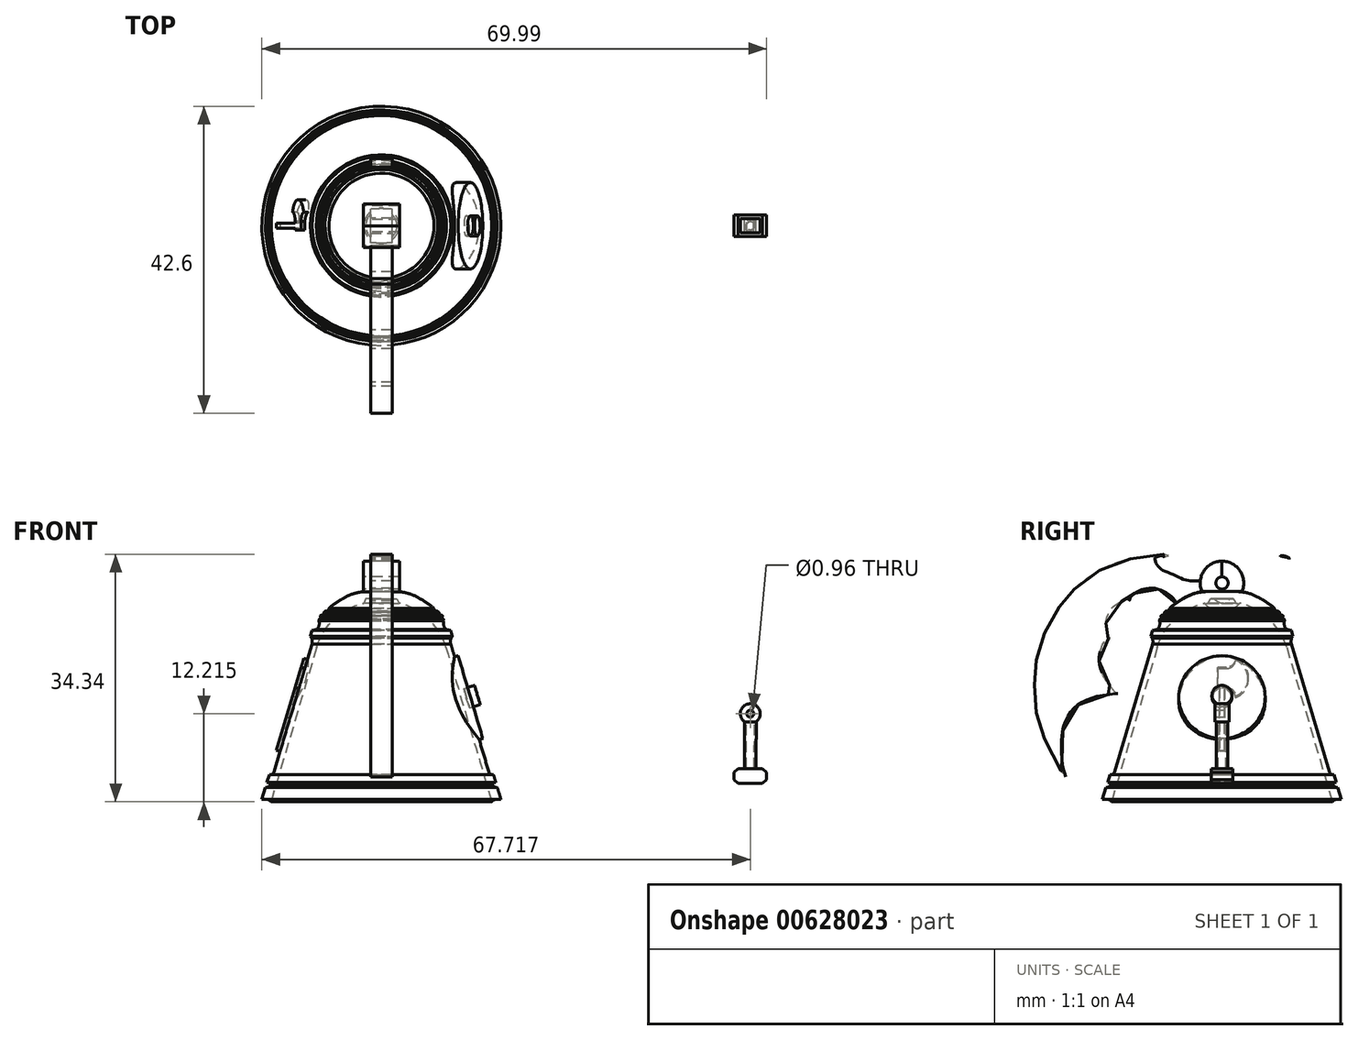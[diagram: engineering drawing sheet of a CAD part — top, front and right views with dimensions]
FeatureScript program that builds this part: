
annotation { "Feature Type Name" : "Feature", "Feature Type Description" : "" }
export const myFeature = defineFeature(function(context is Context, id is Id, definition is map)
    precondition{}
    {
        {
            var Q0;
            Q0=qCreatedBy(makeId("Front.planeOp"),FACE);
            var sketch = newSketch(context, id + "F0", { "sketchPlane" : qUnion([Q0])});
            skLineSegment(sketch, "E0", {"start": v(-8.59, 10.1) * mm, "end": v(-8.67, 9.83) * mm});
            skArc(sketch, "E1", {"start": v(-5.15, 13.04) * mm, "mid": v(-6.25, 12.35) * mm, "end": v(-7.29, 11.58) * mm});
            skFitSpline(sketch, "E2", {"points": [v(-8.38, 10.64) * mm, v(-8.4, 10.62) * mm, v(-8.42, 10.6) * mm, v(-8.44, 10.56) * mm, v(-8.46, 10.52) * mm, v(-8.47, 10.5) * mm], "startDerivative": vector(-0.14, -0.15) * mm, "endDerivative": vector(-0.05, -0.19) * mm});
            skArc(sketch, "E3", {"start": v(-15.49, -15.03) * mm, "mid": v(-15.75, -14.94) * mm, "end": v(-16.03, -14.94) * mm});
            skArc(sketch, "E4", {"start": v(-8.59, 10.1) * mm, "mid": v(-8.44, 10.27) * mm, "end": v(-8.47, 10.5) * mm});
            skLineSegment(sketch, "E5.trimOffspring", {"start": v(0, 13.78) * mm, "end": v(0, -14.94) * mm, "construction": true});
            skLineSegment(sketch, "E6", {"start": v(0, 15.06) * mm, "end": v(0, 13.78) * mm});
            skArc(sketch, "E7", {"start": v(-8.38, 10.64) * mm, "mid": v(-8.09, 10.73) * mm, "end": v(-7.98, 11.01) * mm});
            skLineSegment(sketch, "E8", {"start": v(-16.03, -14.94) * mm, "end": v(-16.32, -14.94) * mm});
            skLineSegment(sketch, "E9.0", {"start": v(-9.09, 10.25) * mm, "end": v(-15.86, -12.55) * mm});
            skLineSegment(sketch, "E10", {"start": v(-16.53, -14.8) * mm, "end": v(-16.58, -14.94) * mm});
            skLineSegment(sketch, "E11", {"start": v(-16.03, -14.94) * mm, "end": v(-16.58, -14.94) * mm});
            skPoint(sketch, "E12.trimOffspring.start.orphan", {"position": v(-15.75, -13.98) * mm});
            skLineSegment(sketch, "E13", {"start": v(-1.94, 13.9) * mm, "end": v(0, 13.89) * mm});
            skLineSegment(sketch, "E14", {"start": v(-2.16, 12.93) * mm, "end": v(0, 12.92) * mm});
            skLineSegment(sketch, "E15", {"start": v(0, 12.92) * mm, "end": v(0, 13.89) * mm});
            skPoint(sketch, "E16.visualSharp", {"position": v(-3.46, 13.9) * mm});
            skArc(sketch, "E16.filletArc", {"start": v(-1.94, 13.9) * mm, "mid": v(-3.6, 13.68) * mm, "end": v(-5.15, 13.04) * mm});
            skPoint(sketch, "E17.visualSharp", {"position": v(-3.46, 12.93) * mm});
            skLineSegment(sketch, "E18", {"start": v(-16.07, -13.24) * mm, "end": v(-15.86, -13.24) * mm});
            skArc(sketch, "E19", {"start": v(-15.86, -13.24) * mm, "mid": v(-15.6, -13.13) * mm, "end": v(-15.43, -12.9) * mm});
            skPoint(sketch, "E20.end.orphan", {"position": v(-16.02, -13.98) * mm});
            skPoint(sketch, "E20.start.orphan", {"position": v(-16.29, -13.98) * mm});
            skLineSegment(sketch, "E21", {"start": v(0, 0) * mm, "end": v(-16.93, 0) * mm, "construction": true});
            skLineSegment(sketch, "E22", {"start": v(-12.13, 0) * mm, "end": v(-12, 0.48) * mm});
            skLineSegment(sketch, "E23", {"start": v(-12, 0.48) * mm, "end": v(-11.72, 0.48) * mm});
            skLineSegment(sketch, "E24", {"start": v(-12.13, 0) * mm, "end": v(-12.28, -0.48) * mm});
            skArc(sketch, "E25", {"start": v(-11.72, 0.48) * mm, "mid": v(-11.51, 0.57) * mm, "end": v(-11.37, 0.74) * mm});
            skLineSegment(sketch, "E26", {"start": v(-11.82, -0.76) * mm, "end": v(-11.82, -0.77) * mm});
            skLineSegment(sketch, "E27", {"start": v(-12.05, -0.63) * mm, "end": v(-12.28, -0.48) * mm});
            skPoint(sketch, "E28.end.orphan", {"position": v(-12.05, -0.63) * mm});
            skArc(sketch, "E29", {"start": v(-11.9, -1.03) * mm, "mid": v(-11.92, -0.81) * mm, "end": v(-12.05, -0.63) * mm});
            skPoint(sketch, "E30.start.orphan", {"position": v(-11.45, 0.48) * mm});
            skLineSegment(sketch, "E31.trimOffspring", {"start": v(-11.9, -1.03) * mm, "end": v(-14.9, -11.12) * mm});
            skLineSegment(sketch, "E32", {"start": v(-11.37, 0.74) * mm, "end": v(-11.9, -1.03) * mm});
            skLineSegment(sketch, "E33", {"start": v(-15.27, -11.46) * mm, "end": v(-15.54, -11.46) * mm});
            skLineSegment(sketch, "E34", {"start": v(-15.59, -12.55) * mm, "end": v(-15.86, -12.55) * mm});
            skArc(sketch, "E35", {"start": v(-15.43, -12.9) * mm, "mid": v(-15.47, -12.7) * mm, "end": v(-15.59, -12.55) * mm});
            skArc(sketch, "E36", {"start": v(-15.27, -11.46) * mm, "mid": v(-15.03, -11.34) * mm, "end": v(-14.9, -11.12) * mm});
            skPoint(sketch, "E37.orphan", {"position": v(-15, -11.46) * mm});
            skLineSegment(sketch, "E38.trimOffspring", {"start": v(-16.07, -13.24) * mm, "end": v(-16.53, -14.8) * mm});
            skArc(sketch, "E39", {"start": v(-7.8, 11.16) * mm, "mid": v(-7.45, 11.26) * mm, "end": v(-7.29, 11.58) * mm});
            skArc(sketch, "E40.trimOffspring", {"start": v(-7.8, 11.16) * mm, "mid": v(-7.89, 11.09) * mm, "end": v(-7.98, 11.01) * mm});
            skArc(sketch, "E41", {"start": v(-9.03, 8.62) * mm, "mid": v(-8.65, 9.17) * mm, "end": v(-8.67, 9.83) * mm});
            skFitSpline(sketch, "E42", {"points": [v(-13.15, -1.1) * mm, v(-13.15, -3.43) * mm], "startDerivative": vector(0, -2.5) * mm, "endDerivative": vector(0, -2.5) * mm});
            skLineSegment(sketch, "E43", {"start": v(0, 18.67) * mm, "end": v(0, 15.06) * mm});
            skLineSegment(sketch, "E44", {"start": v(-9.03, 8.62) * mm, "end": v(-9.6, 8.5) * mm});
            skPoint(sketch, "E45.end.orphan", {"position": v(-9.06, 8.5) * mm});
            skLineSegment(sketch, "E46.trimOffspring", {"start": v(-9.62, 6.63) * mm, "end": v(-11.37, 0.74) * mm});
            skLineSegment(sketch, "E47", {"start": v(-9.85, 7.69) * mm, "end": v(-9.66, 7.42) * mm});
            skArc(sketch, "E48", {"start": v(-9.62, 6.63) * mm, "mid": v(-9.58, 7.03) * mm, "end": v(-9.66, 7.42) * mm});
            skPoint(sketch, "E49.orphan", {"position": v(-9.47, 7.15) * mm});
            skLineSegment(sketch, "E50.0", {"start": v(-8.96, 6.14) * mm, "end": v(-13.88, -10.43) * mm});
            skLineSegment(sketch, "E51", {"start": v(-9.1, 6.5) * mm, "end": v(-8.96, 6.14) * mm});
            skArc(sketch, "E52", {"start": v(-2.44, 12.3) * mm, "mid": v(-6.53, 10.1) * mm, "end": v(-8.96, 6.14) * mm});
            skPoint(sketch, "E53.orphan", {"position": v(-2.83, 12.9) * mm});
            skPoint(sketch, "E54.start.orphan", {"position": v(-5.02, 12.26) * mm});
            skPoint(sketch, "E55.start.orphan", {"position": v(-7.33, 10.84) * mm});
            skPoint(sketch, "E56.0.start.orphan", {"position": v(-8.14, 9.72) * mm});
            skLineSegment(sketch, "E57", {"start": v(-2.16, 12.93) * mm, "end": v(-2.44, 12.3) * mm});
            skArc(sketch, "E58", {"start": v(-1.08, 12.92) * mm, "mid": v(0, 12.3) * mm, "end": v(1.08, 12.92) * mm});
            skLineSegment(sketch, "E59", {"start": v(-13.88, -10.43) * mm, "end": v(-15.32, -15.25) * mm});
            skLineSegment(sketch, "E60", {"start": v(-15.32, -15.25) * mm, "end": v(-15.49, -15.03) * mm});
            skArc(sketch, "E61", {"start": v(51.94, -4.15) * mm, "mid": v(51.14, -1.66) * mm, "end": v(50.33, -4.15) * mm});
            skCircle(sketch, "E62", {"center": v(51.14, -3.04) * mm, "radius": 0.48 * mm});
            skLineSegment(sketch, "E63", {"start": v(50.33, -4.15) * mm, "end": v(50.33, -10.65) * mm});
            skLineSegment(sketch, "E64.bottom", {"start": v(51.14, -12.67) * mm, "end": v(50, -12.67) * mm});
            skLineSegment(sketch, "E64.top", {"start": v(51.14, -10.65) * mm, "end": v(50, -10.65) * mm});
            skLineSegment(sketch, "E64.left", {"start": v(51.14, -12.67) * mm, "end": v(51.14, -10.65) * mm});
            skLineSegment(sketch, "E64.right", {"start": v(48.86, -11.66) * mm, "end": v(48.86, -11.15) * mm});
            skLineSegment(sketch, "E65", {"start": v(-2.27, -8.62) * mm, "end": v(0, -8.62) * mm, "construction": true});
            skLineSegment(sketch, "E66", {"start": v(50, -10.65) * mm, "end": v(50, -12.67) * mm, "construction": true});
            skLineSegment(sketch, "E67", {"start": v(50, -10.65) * mm, "end": v(49.43, -10.65) * mm});
            skLineSegment(sketch, "E68", {"start": v(49.43, -12.67) * mm, "end": v(50, -12.67) * mm});
            skLineSegment(sketch, "E69", {"start": v(49.43, -10.65) * mm, "end": v(48.86, -11.15) * mm});
            skLineSegment(sketch, "E70", {"start": v(48.86, -12.16) * mm, "end": v(49.43, -12.67) * mm});
            skPoint(sketch, "E71.orphan", {"position": v(-2.27, -9.63) * mm});
            skPoint(sketch, "E72.orphan", {"position": v(-2.27, -7.61) * mm});
            skLineSegment(sketch, "E73", {"start": v(48.86, -11.66) * mm, "end": v(48.86, -12.16) * mm});
            skLineSegment(sketch, "E74", {"start": v(50.33, -4.15) * mm, "end": v(51.14, -4.15) * mm});
            skLineSegment(sketch, "E75", {"start": v(50.58, -4.15) * mm, "end": v(50.58, -10.65) * mm});
            skLineSegment(sketch, "E76.MirrorCS", {"start": v(53.41, -11.66) * mm, "end": v(53.41, -11.15) * mm});
            skLineSegment(sketch, "E77.MirrorCS", {"start": v(53.41, -11.66) * mm, "end": v(53.41, -12.16) * mm});
            skLineSegment(sketch, "E78.MirrorCS", {"start": v(53.41, -12.16) * mm, "end": v(52.84, -12.67) * mm});
            skLineSegment(sketch, "E79.MirrorCS", {"start": v(52.84, -12.67) * mm, "end": v(52.27, -12.67) * mm});
            skLineSegment(sketch, "E80.MirrorCS", {"start": v(51.14, -12.67) * mm, "end": v(52.27, -12.67) * mm});
            skLineSegment(sketch, "E81.MirrorCS", {"start": v(51.14, -10.65) * mm, "end": v(52.27, -10.65) * mm});
            skLineSegment(sketch, "E82.MirrorCS", {"start": v(52.84, -10.65) * mm, "end": v(53.41, -11.15) * mm});
            skLineSegment(sketch, "E83.MirrorCS", {"start": v(52.27, -10.65) * mm, "end": v(52.84, -10.65) * mm});
            skLineSegment(sketch, "E84", {"start": v(51.14, -4.15) * mm, "end": v(51.94, -4.15) * mm});
            skLineSegment(sketch, "E85", {"start": v(51.15, -4.17) * mm, "end": v(51.14, -10.65) * mm, "construction": true});
            skFitSpline(sketch, "E86.MirrorCS", {"points": [v(8.38, 10.64) * mm, v(8.4, 10.62) * mm, v(8.42, 10.6) * mm, v(8.44, 10.56) * mm, v(8.46, 10.52) * mm, v(8.47, 10.5) * mm], "startDerivative": vector(0.14, -0.15) * mm, "endDerivative": vector(0.05, -0.19) * mm});
            skArc(sketch, "E87.MirrorCS", {"start": v(7.8, 11.16) * mm, "mid": v(7.89, 11.09) * mm, "end": v(7.98, 11.01) * mm});
            skArc(sketch, "E88.MirrorCS", {"start": v(8.59, 10.1) * mm, "mid": v(8.44, 10.27) * mm, "end": v(8.47, 10.5) * mm});
            skLineSegment(sketch, "E89.MirrorCS", {"start": v(8.59, 10.1) * mm, "end": v(8.67, 9.83) * mm});
            skArc(sketch, "E90.MirrorCS", {"start": v(8.38, 10.64) * mm, "mid": v(8.09, 10.73) * mm, "end": v(7.98, 11.01) * mm});
            skLineSegment(sketch, "E91.MirrorCS", {"start": v(11.82, -0.76) * mm, "end": v(11.82, -0.77) * mm});
            skLineSegment(sketch, "E92.MirrorCS", {"start": v(11.37, 0.74) * mm, "end": v(11.9, -1.03) * mm});
            skLineSegment(sketch, "E93.MirrorCS", {"start": v(12.13, 0) * mm, "end": v(12.28, -0.48) * mm});
            skArc(sketch, "E94.MirrorCS", {"start": v(11.72, 0.48) * mm, "mid": v(11.51, 0.57) * mm, "end": v(11.37, 0.74) * mm});
            skLineSegment(sketch, "E95.MirrorCS", {"start": v(12.05, -0.63) * mm, "end": v(12.28, -0.48) * mm});
            skArc(sketch, "E96.MirrorCS", {"start": v(11.9, -1.03) * mm, "mid": v(11.92, -0.81) * mm, "end": v(12.05, -0.63) * mm});
            skLineSegment(sketch, "E97.MirrorCS", {"start": v(16.07, -13.24) * mm, "end": v(15.86, -13.24) * mm});
            skLineSegment(sketch, "E98.MirrorCS", {"start": v(12.13, 0) * mm, "end": v(12, 0.48) * mm});
            skLineSegment(sketch, "E99.MirrorCS", {"start": v(12, 0.48) * mm, "end": v(11.72, 0.48) * mm});
            skLineSegment(sketch, "E100.MirrorCS", {"start": v(9.03, 8.62) * mm, "end": v(9.6, 8.5) * mm});
            skArc(sketch, "E101.MirrorCS", {"start": v(15.49, -15.03) * mm, "mid": v(15.75, -14.94) * mm, "end": v(16.03, -14.94) * mm});
            skArc(sketch, "E102.MirrorCS", {"start": v(15.86, -13.24) * mm, "mid": v(15.6, -13.13) * mm, "end": v(15.43, -12.9) * mm});
            skLineSegment(sketch, "E103.MirrorCS", {"start": v(15.27, -11.46) * mm, "end": v(15.54, -11.46) * mm});
            skArc(sketch, "E104.MirrorCS", {"start": v(9.03, 8.62) * mm, "mid": v(8.65, 9.17) * mm, "end": v(8.67, 9.83) * mm});
            skLineSegment(sketch, "E105.MirrorCS", {"start": v(9.85, 7.69) * mm, "end": v(9.66, 7.42) * mm});
            skArc(sketch, "E106.MirrorCS", {"start": v(15.43, -12.9) * mm, "mid": v(15.47, -12.7) * mm, "end": v(15.59, -12.55) * mm});
            skArc(sketch, "E107.MirrorCS", {"start": v(15.27, -11.46) * mm, "mid": v(15.03, -11.34) * mm, "end": v(14.9, -11.12) * mm});
            skLineSegment(sketch, "E108.MirrorCS", {"start": v(16.03, -14.94) * mm, "end": v(16.58, -14.94) * mm});
            skLineSegment(sketch, "E109.MirrorCS", {"start": v(16.03, -14.94) * mm, "end": v(16.32, -14.94) * mm});
            skLineSegment(sketch, "E110.MirrorCS", {"start": v(9.1, 6.5) * mm, "end": v(8.96, 6.14) * mm});
            skLineSegment(sketch, "E111.MirrorCS", {"start": v(16.07, -13.24) * mm, "end": v(16.53, -14.8) * mm});
            skLineSegment(sketch, "E112.MirrorCS", {"start": v(16.53, -14.8) * mm, "end": v(16.58, -14.94) * mm});
            skLineSegment(sketch, "E113.MirrorCS", {"start": v(15.59, -12.55) * mm, "end": v(15.86, -12.55) * mm});
            skArc(sketch, "E114.MirrorCS", {"start": v(9.62, 6.63) * mm, "mid": v(9.58, 7.03) * mm, "end": v(9.66, 7.42) * mm});
            skLineSegment(sketch, "E115.MirrorCS", {"start": v(2.16, 12.93) * mm, "end": v(2.44, 12.3) * mm});
            skLineSegment(sketch, "E116.MirrorCS", {"start": v(15.32, -15.25) * mm, "end": v(15.49, -15.03) * mm});
            skArc(sketch, "E117.MirrorCS", {"start": v(7.8, 11.16) * mm, "mid": v(7.45, 11.26) * mm, "end": v(7.29, 11.58) * mm});
            skLineSegment(sketch, "E118.MirrorCS", {"start": v(2.16, 12.93) * mm, "end": v(0, 12.92) * mm});
            skFitSpline(sketch, "E119.MirrorCS", {"points": [v(13.15, -1.1) * mm, v(13.15, -3.43) * mm], "startDerivative": vector(0, -2.5) * mm, "endDerivative": vector(0, -2.5) * mm});
            skArc(sketch, "E120.MirrorCS", {"start": v(1.94, 13.9) * mm, "mid": v(3.6, 13.68) * mm, "end": v(5.15, 13.04) * mm});
            skPoint(sketch, "E121.MirrorP", {"position": v(9.06, 8.5) * mm});
            skPoint(sketch, "E122.MirrorP", {"position": v(7.33, 10.84) * mm});
            skPoint(sketch, "E123.MirrorP", {"position": v(3.46, 12.93) * mm});
            skPoint(sketch, "E124.MirrorP", {"position": v(11.45, 0.48) * mm});
            skLineSegment(sketch, "E125.MirrorCS", {"start": v(9.62, 6.63) * mm, "end": v(11.37, 0.74) * mm});
            skPoint(sketch, "E126.MirrorP", {"position": v(15.75, -13.98) * mm});
            skLineSegment(sketch, "E127.MirrorCS", {"start": v(13.88, -10.43) * mm, "end": v(15.32, -15.25) * mm});
            skLineSegment(sketch, "E128.MirrorCS", {"start": v(8.96, 6.14) * mm, "end": v(13.88, -10.43) * mm});
            skArc(sketch, "E129.MirrorCS", {"start": v(2.44, 12.3) * mm, "mid": v(6.53, 10.1) * mm, "end": v(8.96, 6.14) * mm});
            skPoint(sketch, "E130.MirrorP", {"position": v(8.14, 9.72) * mm});
            skPoint(sketch, "E131.MirrorP", {"position": v(16.29, -13.98) * mm});
            skPoint(sketch, "E132.MirrorP", {"position": v(9.47, 7.15) * mm});
            skPoint(sketch, "E133.MirrorP", {"position": v(12.05, -0.63) * mm});
            skPoint(sketch, "E134.MirrorP", {"position": v(15, -11.46) * mm});
            skArc(sketch, "E135.MirrorCS", {"start": v(5.15, 13.04) * mm, "mid": v(6.25, 12.35) * mm, "end": v(7.29, 11.58) * mm});
            skPoint(sketch, "E136.MirrorP", {"position": v(5.02, 12.26) * mm});
            skLineSegment(sketch, "E137.MirrorCS", {"start": v(0, 0) * mm, "end": v(16.93, 0) * mm, "construction": true});
            skLineSegment(sketch, "E138.MirrorCS", {"start": v(2.27, -8.62) * mm, "end": v(0, -8.62) * mm, "construction": true});
            skPoint(sketch, "E139.MirrorP", {"position": v(3.46, 13.9) * mm});
            skPoint(sketch, "E140.MirrorP", {"position": v(2.27, -7.61) * mm});
            skPoint(sketch, "E141.MirrorP", {"position": v(2.83, 12.9) * mm});
            skLineSegment(sketch, "E142.MirrorCS", {"start": v(11.9, -1.03) * mm, "end": v(14.9, -11.12) * mm});
            skPoint(sketch, "E143.MirrorP", {"position": v(16.02, -13.98) * mm});
            skLineSegment(sketch, "E144.MirrorCS", {"start": v(1.94, 13.9) * mm, "end": v(0, 13.89) * mm});
            skLineSegment(sketch, "E145.MirrorCS", {"start": v(9.09, 10.25) * mm, "end": v(15.86, -12.55) * mm});
            skPoint(sketch, "E146.MirrorP", {"position": v(2.27, -9.63) * mm});
            skSolve(sketch);
        }
        {
            var Q0;
            Q0=makeQuery(id+"F0.imprint","IMPRINT",FACE,{"disambiguationData":[TD([[makeQuery(id+"F0.imprint","IMPRINT",EDGE,{"derivedFrom":sQuery(id+"F0.wireOp",EDGE,"E0")}),1.0]])]});
            var Q1;
            Q1=sQuery(id+"F0.wireOp",EDGE,"E5.trimOffspring");
            revolve(context, id + "F1", {"entities" : qUnion([Q0]), "axis" : qUnion([Q1]), "revolveType" : RevolveType.FULL});
        }
        {
            var Q0;
            Q0=sQuery(id+"F0.wireOp",EDGE,"E9.0");
            cPlane(context, id + "F2", {"entities" : qUnion([Q0]), "cplaneType" : CPlaneType.LINE_ANGLE, "offset" : 25 * mm, "angle" : 0 * degree, "width" : 150 * mm, "height" : 150 * mm});
        }
        {
            var Q0;
            Q0=qCreatedBy(id+"F2.planeOp",FACE);
            var sketch = newSketch(context, id + "F3", { "sketchPlane" : qUnion([Q0])});
            skLineSegment(sketch, "E147", {"start": v(0, 4.01) * mm, "end": v(0, -16.17) * mm, "construction": true});
            skPoint(sketch, "E148.end.orphan", {"position": v(0, -15) * mm});
            skLineSegment(sketch, "E149", {"start": v(-0.34, -9.4) * mm, "end": v(-0.34, -2.82) * mm});
            skLineSegment(sketch, "E150", {"start": v(-0.34, 0.07) * mm, "end": v(0, 0.07) * mm});
            skLineSegment(sketch, "E151.bottom", {"start": v(0, 0.07) * mm, "end": v(-0.6, 0.07) * mm});
            skLineSegment(sketch, "E151.top", {"start": v(0, -2.82) * mm, "end": v(-0.6, -2.82) * mm});
            skLineSegment(sketch, "E151.left", {"start": v(0, 0.07) * mm, "end": v(0, -2.82) * mm});
            skLineSegment(sketch, "E151.right", {"start": v(-0.6, 0.07) * mm, "end": v(-0.6, -2.82) * mm});
            skArc(sketch, "E152", {"start": v(-1.87, 1.37) * mm, "mid": v(-3.63, -1.38) * mm, "end": v(-1.87, -4.12) * mm});
            skArc(sketch, "E153", {"start": v(-1.87, 1.37) * mm, "mid": v(-1.5, 0.46) * mm, "end": v(-0.6, 0.07) * mm});
            skArc(sketch, "E154", {"start": v(-0.6, -2.82) * mm, "mid": v(-1.5, -3.21) * mm, "end": v(-1.87, -4.12) * mm});
            skArc(sketch, "E155.MirrorCS", {"start": v(0.6, -2.82) * mm, "mid": v(1.5, -3.21) * mm, "end": v(1.87, -4.12) * mm});
            skLineSegment(sketch, "E156.MirrorCS", {"start": v(0.34, -9.4) * mm, "end": v(0.34, -2.82) * mm});
            skLineSegment(sketch, "E157.MirrorCS", {"start": v(0, -2.82) * mm, "end": v(0.6, -2.82) * mm});
            skLineSegment(sketch, "E158.MirrorCS", {"start": v(0, 0.07) * mm, "end": v(0.6, 0.07) * mm});
            skLineSegment(sketch, "E159.MirrorCS", {"start": v(0.6, 0.07) * mm, "end": v(0.6, -2.82) * mm});
            skArc(sketch, "E160.MirrorCS", {"start": v(1.87, 1.37) * mm, "mid": v(1.5, 0.46) * mm, "end": v(0.6, 0.07) * mm});
            skArc(sketch, "E161.MirrorCS", {"start": v(1.87, 1.37) * mm, "mid": v(3.63, -1.38) * mm, "end": v(1.87, -4.12) * mm});
            skLineSegment(sketch, "E162", {"start": v(-0.34, -9.4) * mm, "end": v(-0.34, -11.91) * mm});
            skLineSegment(sketch, "E163", {"start": v(0.34, -9.4) * mm, "end": v(0.34, -11.91) * mm});
            skLineSegment(sketch, "E164", {"start": v(0.34, -11.91) * mm, "end": v(-0.34, -11.91) * mm});
            skSolve(sketch);
        }
        {
            var Q0;
            Q0=makeQuery(id+"F3.imprint","IMPRINT",FACE,{"disambiguationData":[TD([[makeQuery(id+"F3.imprint","IMPRINT",EDGE,{"derivedFrom":sQuery(id+"F3.wireOp",EDGE,"E151.right")}),-1.0]])]});
            var Q1;
            Q1=makeQuery(id+"F3.imprint","IMPRINT",FACE,{"disambiguationData":[TD([[makeQuery(id+"F3.imprint","IMPRINT",EDGE,{"derivedFrom":sQuery(id+"F3.wireOp",EDGE,"E155.MirrorCS")}),1.0]])]});
            var Q2;
            {var subQ0=sQuery(id+"F3.wireOp",EDGE,"E151.left");Q2=makeQuery(id+"F3.imprint","IMPRINT",FACE,{"disambiguationData":[TD([[makeQuery(id+"F3.imprint","IMPRINT",EDGE,{"derivedFrom":subQ0}),-1.0]])]});}
            var Q3;
            {var subQ3=sQuery(id+"F3.wireOp",EDGE,"E151.left");Q3=makeQuery(id+"F3.imprint","IMPRINT",FACE,{"disambiguationData":[TD([[makeQuery(id+"F3.imprint","IMPRINT",EDGE,{"derivedFrom":subQ3}),1.0]])]});}
            var Q4;
            Q4=makeQuery(id+"F3.imprint","IMPRINT",FACE,{"disambiguationData":[TD([[makeQuery(id+"F3.imprint","IMPRINT",EDGE,{"derivedFrom":sQuery(id+"F3.wireOp",EDGE,"Z1JNySv2-YXMW-AunD-5vYt-RYXNe48j4Wng")}),-1.0]])]});
            var Q5;
            {var subQ4=sQuery(id+"F3.wireOp",EDGE,"E149");Q5=makeQuery(id+"F3.imprint","IMPRINT",FACE,{"disambiguationData":[TD([[makeQuery(id+"F3.imprint","IMPRINT",EDGE,{"derivedFrom":subQ4}),-1.0]])]});}
            extrude(context, id + "F4", {"entities" : qUnion([Q0, Q1, Q2, Q3, Q4, Q5]), "endBound" : BoundingType.UP_TO_NEXT, "oppositeDirection" : true, "depth" : 4 * mm, "offsetDistance" : 25 * mm});
        }
        {
            var Q0;
            {var subQ0=sQuery(id+"F0.wireOp",EDGE,"E63");Q0=makeQuery(id+"F0.imprint","IMPRINT",FACE,{"disambiguationData":[TD([[makeQuery(id+"F0.imprint","IMPRINT",EDGE,{"derivedFrom":subQ0}),1.0]])]});}
            var Q1;
            Q1=sQuery(id+"F0.wireOp",EDGE,"E85");
            revolve(context, id + "F5", {"entities" : qUnion([Q0]), "axis" : qUnion([Q1]), "revolveType" : RevolveType.FULL});
        }
        {
            var Q0;
            Q0=makeQuery(id+"F0.imprint","IMPRINT",FACE,{"disambiguationData":[TD([[makeQuery(id+"F0.imprint","IMPRINT",EDGE,{"derivedFrom":sQuery(id+"F0.wireOp",EDGE,"E64.left")}),-1.0]])]});
            var Q1;
            Q1=makeQuery(id+"F0.imprint","IMPRINT",FACE,{"disambiguationData":[TD([[makeQuery(id+"F0.imprint","IMPRINT",EDGE,{"derivedFrom":sQuery(id+"F0.wireOp",EDGE,"E64.bottom")}),-1.0]])]});
            extrude(context, id + "F6", {"entities" : qUnion([Q0, Q1]), "operationType" : NewBodyOperationType.ADD, "endBound" : BoundingType.SYMMETRIC, "depth" : 3 * mm, "offsetDistance" : 25 * mm});
        }
        {
            var Q0;
            {var subQ1=sQuery(id+"F0.wireOp",EDGE,"E61");Q0=makeQuery(id+"F0.imprint","IMPRINT",FACE,{"disambiguationData":[TD([[makeQuery(id+"F0.imprint","IMPRINT",EDGE,{"derivedFrom":subQ1}),1.0]])]});}
            extrude(context, id + "F7", {"entities" : qUnion([Q0]), "operationType" : NewBodyOperationType.ADD, "endBound" : BoundingType.SYMMETRIC, "depth" : 2 * mm, "offsetDistance" : 25 * mm});
        }
        {
            var Q0;
            Q0=qCreatedBy(makeId("Right.planeOp"),FACE);
            var sketch = newSketch(context, id + "F8", { "sketchPlane" : qUnion([Q0])});
            skLineSegment(sketch, "E165", {"start": v(-8.59, 10.13) * mm, "end": v(-8.67, 9.86) * mm});
            skArc(sketch, "E166", {"start": v(-5.15, 13.07) * mm, "mid": v(-6.25, 12.38) * mm, "end": v(-7.29, 11.61) * mm});
            skFitSpline(sketch, "E167", {"points": [v(-8.38, 10.67) * mm, v(-8.4, 10.65) * mm, v(-8.42, 10.63) * mm, v(-8.44, 10.6) * mm, v(-8.46, 10.55) * mm, v(-8.47, 10.52) * mm], "startDerivative": vector(-0.14, -0.15) * mm, "endDerivative": vector(-0.05, -0.19) * mm});
            skArc(sketch, "E168", {"start": v(-15.49, -15) * mm, "mid": v(-15.75, -14.91) * mm, "end": v(-16.03, -14.91) * mm});
            skArc(sketch, "E169", {"start": v(-8.59, 10.13) * mm, "mid": v(-8.44, 10.3) * mm, "end": v(-8.47, 10.52) * mm});
            skLineSegment(sketch, "E170.trimOffspring", {"start": v(0, 13.8) * mm, "end": v(0, -14.91) * mm, "construction": true});
            skLineSegment(sketch, "E171", {"start": v(0, 15.09) * mm, "end": v(0, 13.8) * mm});
            skArc(sketch, "E172", {"start": v(-8.38, 10.67) * mm, "mid": v(-8.09, 10.76) * mm, "end": v(-7.98, 11.04) * mm});
            skLineSegment(sketch, "E173", {"start": v(-16.03, -14.91) * mm, "end": v(-16.32, -14.91) * mm});
            skLineSegment(sketch, "E174.0", {"start": v(-9.09, 10.28) * mm, "end": v(-15.86, -12.52) * mm});
            skLineSegment(sketch, "E175", {"start": v(-16.53, -14.77) * mm, "end": v(-16.58, -14.91) * mm});
            skLineSegment(sketch, "E176", {"start": v(-16.03, -14.91) * mm, "end": v(-16.58, -14.91) * mm});
            skPoint(sketch, "E177.trimOffspring.start.orphan", {"position": v(-15.75, -13.95) * mm});
            skLineSegment(sketch, "E178", {"start": v(-1.94, 13.93) * mm, "end": v(0, 13.92) * mm});
            skLineSegment(sketch, "E179", {"start": v(-2.16, 12.96) * mm, "end": v(0, 12.95) * mm});
            skLineSegment(sketch, "E180", {"start": v(0, 12.95) * mm, "end": v(0, 13.92) * mm});
            skPoint(sketch, "E181.visualSharp", {"position": v(-3.46, 13.93) * mm});
            skArc(sketch, "E181.filletArc", {"start": v(-1.94, 13.93) * mm, "mid": v(-3.6, 13.71) * mm, "end": v(-5.15, 13.07) * mm});
            skPoint(sketch, "E182.visualSharp", {"position": v(-3.46, 12.96) * mm});
            skLineSegment(sketch, "E183", {"start": v(-16.07, -13.2) * mm, "end": v(-15.86, -13.2) * mm});
            skArc(sketch, "E184", {"start": v(-15.86, -13.2) * mm, "mid": v(-15.6, -13.1) * mm, "end": v(-15.43, -12.87) * mm});
            skPoint(sketch, "E185.end.orphan", {"position": v(-16.02, -13.95) * mm});
            skPoint(sketch, "E185.start.orphan", {"position": v(-16.29, -13.95) * mm});
            skLineSegment(sketch, "E186", {"start": v(0, 0.03) * mm, "end": v(-16.93, 0.03) * mm, "construction": true});
            skLineSegment(sketch, "E187", {"start": v(-12.13, 0.03) * mm, "end": v(-12, 0.5) * mm});
            skLineSegment(sketch, "E188", {"start": v(-12, 0.5) * mm, "end": v(-11.72, 0.5) * mm});
            skLineSegment(sketch, "E189", {"start": v(-12.13, 0.03) * mm, "end": v(-12.28, -0.45) * mm});
            skArc(sketch, "E190", {"start": v(-11.72, 0.5) * mm, "mid": v(-11.51, 0.6) * mm, "end": v(-11.37, 0.77) * mm});
            skLineSegment(sketch, "E191", {"start": v(-11.82, -0.73) * mm, "end": v(-11.82, -0.74) * mm});
            skLineSegment(sketch, "E192", {"start": v(-12.05, -0.6) * mm, "end": v(-12.28, -0.45) * mm});
            skPoint(sketch, "E193.end.orphan", {"position": v(-12.05, -0.6) * mm});
            skArc(sketch, "E194", {"start": v(-11.9, -1) * mm, "mid": v(-11.92, -0.78) * mm, "end": v(-12.05, -0.6) * mm});
            skPoint(sketch, "E195.start.orphan", {"position": v(-11.45, 0.5) * mm});
            skLineSegment(sketch, "E196.trimOffspring", {"start": v(-11.9, -1) * mm, "end": v(-14.9, -11.09) * mm});
            skLineSegment(sketch, "E197", {"start": v(-11.37, 0.77) * mm, "end": v(-11.9, -1) * mm});
            skLineSegment(sketch, "E198", {"start": v(-15.27, -11.43) * mm, "end": v(-15.54, -11.43) * mm});
            skLineSegment(sketch, "E199", {"start": v(-15.59, -12.52) * mm, "end": v(-15.86, -12.52) * mm});
            skArc(sketch, "E200", {"start": v(-15.43, -12.87) * mm, "mid": v(-15.47, -12.68) * mm, "end": v(-15.59, -12.52) * mm});
            skArc(sketch, "E201", {"start": v(-15.27, -11.43) * mm, "mid": v(-15.03, -11.31) * mm, "end": v(-14.9, -11.09) * mm});
            skPoint(sketch, "E202.orphan", {"position": v(-15, -11.43) * mm});
            skLineSegment(sketch, "E203.trimOffspring", {"start": v(-16.07, -13.2) * mm, "end": v(-16.53, -14.77) * mm});
            skArc(sketch, "E204", {"start": v(-7.8, 11.2) * mm, "mid": v(-7.45, 11.29) * mm, "end": v(-7.29, 11.61) * mm});
            skArc(sketch, "E205.trimOffspring", {"start": v(-7.8, 11.2) * mm, "mid": v(-7.89, 11.12) * mm, "end": v(-7.98, 11.04) * mm});
            skArc(sketch, "E206", {"start": v(-9.03, 8.65) * mm, "mid": v(-8.65, 9.2) * mm, "end": v(-8.67, 9.86) * mm});
            skFitSpline(sketch, "E207", {"points": [v(-13.15, -1.08) * mm, v(-13.15, -3.4) * mm], "startDerivative": vector(0, -2.5) * mm, "endDerivative": vector(0, -2.5) * mm});
            skLineSegment(sketch, "E208", {"start": v(0, 18.7) * mm, "end": v(0, 15.09) * mm});
            skLineSegment(sketch, "E209", {"start": v(-9.03, 8.65) * mm, "end": v(-9.6, 8.54) * mm});
            skPoint(sketch, "E210.end.orphan", {"position": v(-9.06, 8.54) * mm});
            skLineSegment(sketch, "E211.trimOffspring", {"start": v(-9.62, 6.66) * mm, "end": v(-11.37, 0.77) * mm});
            skLineSegment(sketch, "E212", {"start": v(-9.85, 7.72) * mm, "end": v(-9.66, 7.45) * mm});
            skArc(sketch, "E213", {"start": v(-9.62, 6.66) * mm, "mid": v(-9.58, 7.06) * mm, "end": v(-9.66, 7.45) * mm});
            skPoint(sketch, "E214.orphan", {"position": v(-9.47, 7.18) * mm});
            skLineSegment(sketch, "E215.0", {"start": v(-8.96, 6.17) * mm, "end": v(-13.88, -10.4) * mm});
            skLineSegment(sketch, "E216", {"start": v(-9.1, 6.52) * mm, "end": v(-8.96, 6.17) * mm});
            skArc(sketch, "E217", {"start": v(-2.44, 12.32) * mm, "mid": v(-6.53, 10.13) * mm, "end": v(-8.96, 6.17) * mm});
            skPoint(sketch, "E218.orphan", {"position": v(-2.83, 12.93) * mm});
            skPoint(sketch, "E219.start.orphan", {"position": v(-5.02, 12.29) * mm});
            skPoint(sketch, "E220.start.orphan", {"position": v(-7.33, 10.87) * mm});
            skPoint(sketch, "E221.0.start.orphan", {"position": v(-8.14, 9.75) * mm});
            skLineSegment(sketch, "E222", {"start": v(-2.16, 12.96) * mm, "end": v(-2.44, 12.32) * mm});
            skArc(sketch, "E223", {"start": v(-1.08, 12.95) * mm, "mid": v(0, 12.33) * mm, "end": v(1.08, 12.95) * mm});
            skLineSegment(sketch, "E224", {"start": v(-13.88, -10.4) * mm, "end": v(-15.32, -15.22) * mm});
            skLineSegment(sketch, "E225", {"start": v(-15.32, -15.22) * mm, "end": v(-15.49, -15) * mm});
            skLineSegment(sketch, "E226", {"start": v(-2.27, -8.6) * mm, "end": v(0, -8.6) * mm, "construction": true});
            skPoint(sketch, "E227.orphan", {"position": v(-2.27, -9.6) * mm});
            skPoint(sketch, "E228.orphan", {"position": v(-2.27, -7.58) * mm});
            skArc(sketch, "E229", {"start": v(0, 18.1) * mm, "mid": v(-2.53, 16.74) * mm, "end": v(-2.77, 13.88) * mm});
            skCircle(sketch, "E230", {"center": v(0, 15.09) * mm, "radius": 0.85 * mm});
            skFitSpline(sketch, "E231", {"points": [v(-3, 15.4) * mm, v(-3.67, 15.4) * mm, v(-4.22, 15.38) * mm, v(-4.98, 15.48) * mm, v(-5.98, 15.87) * mm, v(-7.25, 16.46) * mm, v(-8.3, 16.92) * mm, v(-8.8, 17.35) * mm, v(-9.17, 17.85) * mm, v(-9.28, 18.38) * mm, v(-9.26, 18.6) * mm, v(-8.1, 18.83) * mm, v(-8.18, 18.49) * mm, v(-7.68, 18.6) * mm, v(-7.3, 19.05) * mm, v(-7.42, 19.08) * mm, v(-8.36, 19.07) * mm, v(-11.29, 18.68) * mm, v(-13.07, 18.36) * mm, v(-15.24, 17.66) * mm, v(-17.6, 16.44) * mm, v(-19.52, 15.06) * mm, v(-20.68, 14.05) * mm, v(-21.64, 12.97) * mm, v(-22.19, 12.29) * mm, v(-22.95, 11.24) * mm, v(-23.9, 9.6) * mm, v(-24.87, 7.46) * mm, v(-25.3, 6.13) * mm, v(-25.74, 4.27) * mm, v(-25.92, 2.9) * mm, v(-26.01, 1.74) * mm, v(-25.98, 0.23) * mm, v(-25.86, -1.54) * mm, v(-25.67, -3.29) * mm, v(-25.3, -4.85) * mm, v(-24.7, -6.3) * mm, v(-23.49, -8.96) * mm, v(-22.16, -11.2) * mm, v(-21.69, -11.8) * mm, v(-21.8, -11.4) * mm, v(-22.21, -9.27) * mm, v(-22.23, -6.58) * mm, v(-22.08, -5.36) * mm, v(-21.33, -3.32) * mm, v(-20.15, -1.95) * mm, v(-18.51, -1.03) * mm, v(-16.23, -0.44) * mm, v(-14.42, -0.22) * mm, v(-14.66, -0.16) * mm, v(-15.35, 0.6) * mm, v(-16.01, 1.48) * mm, v(-16.8, 3.08) * mm, v(-17.03, 4.61) * mm, v(-16.79, 5.98) * mm, v(-16.08, 7.14) * mm, v(-15.46, 7.46) * mm, v(-15.64, 7.56) * mm, v(-15.92, 8.25) * mm, v(-16.1, 9.53) * mm, v(-15.66, 11.04) * mm, v(-14.71, 12.08) * mm, v(-12.92, 12.78) * mm, v(-12.82, 12.63) * mm, v(-12.8, 12.8) * mm, v(-12.53, 13.26) * mm, v(-11.32, 14.08) * mm, v(-10.28, 14.35) * mm, v(-8.88, 14.25) * mm, v(-7.35, 13.47) * mm, v(-6.57, 12.71) * mm, v(-6.37, 12.3) * mm], "startDerivative": vector(-66.18, 0.33) * mm, "endDerivative": vector(17.3, -46.6) * mm});
            skFitSpline(sketch, "E232", {"points": [v(-9.28, 18.38) * mm, v(-9.28, 18.5) * mm, v(-9.03, 18.62) * mm, v(-8.23, 18.78) * mm, v(-8.08, 18.75) * mm, v(-8.1, 18.7) * mm], "startDerivative": vector(-0.18, 0.89) * mm, "endDerivative": vector(-0.35, -0.57) * mm});
            skFitSpline(sketch, "E233", {"points": [v(-3, 15.4) * mm, v(-3.67, 15.4) * mm, v(-4.22, 15.38) * mm, v(-4.98, 15.48) * mm, v(-5.98, 15.87) * mm, v(-7.25, 16.46) * mm, v(-8.3, 16.92) * mm, v(-8.8, 17.35) * mm, v(-9.17, 17.85) * mm, v(-9.28, 18.38) * mm, v(-9.26, 18.6) * mm, v(-8.1, 18.83) * mm, v(-8.18, 18.49) * mm, v(-7.68, 18.6) * mm, v(-7.3, 19.05) * mm, v(-7.42, 19.08) * mm, v(-8.36, 19.07) * mm, v(-11.29, 18.68) * mm, v(-13.07, 18.36) * mm, v(-15.24, 17.66) * mm, v(-17.6, 16.44) * mm, v(-19.52, 15.06) * mm, v(-20.68, 14.05) * mm, v(-21.64, 12.97) * mm, v(-22.19, 12.29) * mm, v(-22.95, 11.24) * mm, v(-23.9, 9.6) * mm, v(-24.87, 7.46) * mm, v(-25.3, 6.13) * mm, v(-25.74, 4.27) * mm, v(-25.92, 2.9) * mm, v(-26.01, 1.74) * mm, v(-25.98, 0.23) * mm, v(-25.86, -1.54) * mm, v(-25.67, -3.29) * mm, v(-25.3, -4.85) * mm, v(-24.7, -6.3) * mm, v(-23.49, -8.96) * mm, v(-22.16, -11.2) * mm, v(-21.69, -11.8) * mm, v(-21.8, -11.4) * mm, v(-22.21, -9.27) * mm, v(-22.23, -6.58) * mm, v(-22.08, -5.36) * mm, v(-21.33, -3.32) * mm, v(-20.15, -1.95) * mm, v(-18.51, -1.03) * mm, v(-16.23, -0.44) * mm, v(-14.42, -0.22) * mm, v(-14.66, -0.16) * mm, v(-15.35, 0.6) * mm, v(-16.01, 1.48) * mm, v(-16.8, 3.08) * mm, v(-17.03, 4.61) * mm, v(-16.79, 5.98) * mm, v(-16.08, 7.14) * mm, v(-15.46, 7.46) * mm, v(-15.64, 7.56) * mm, v(-15.92, 8.25) * mm, v(-16.1, 9.53) * mm, v(-15.66, 11.04) * mm, v(-14.71, 12.08) * mm, v(-12.92, 12.78) * mm, v(-12.82, 12.63) * mm, v(-12.8, 12.8) * mm, v(-12.53, 13.26) * mm, v(-11.32, 14.08) * mm, v(-10.28, 14.35) * mm, v(-8.88, 14.25) * mm, v(-7.35, 13.47) * mm, v(-6.57, 12.71) * mm, v(-6.37, 12.3) * mm], "startDerivative": vector(-66.18, 0.33) * mm, "endDerivative": vector(17.3, -46.6) * mm});
            skFitSpline(sketch, "E234.MirrorCS", {"points": [v(9.28, 18.38) * mm, v(9.28, 18.5) * mm, v(9.03, 18.62) * mm, v(8.23, 18.78) * mm, v(8.08, 18.75) * mm, v(8.1, 18.7) * mm], "startDerivative": vector(0.18, 0.89) * mm, "endDerivative": vector(0.35, -0.57) * mm});
            skFitSpline(sketch, "E235.MirrorCS", {"points": [v(8.38, 10.67) * mm, v(8.4, 10.65) * mm, v(8.42, 10.63) * mm, v(8.44, 10.6) * mm, v(8.46, 10.55) * mm, v(8.47, 10.52) * mm], "startDerivative": vector(0.14, -0.15) * mm, "endDerivative": vector(0.05, -0.19) * mm});
            skArc(sketch, "E236.MirrorCS", {"start": v(8.38, 10.67) * mm, "mid": v(8.09, 10.76) * mm, "end": v(7.98, 11.04) * mm});
            skLineSegment(sketch, "E237.MirrorCS", {"start": v(11.82, -0.73) * mm, "end": v(11.82, -0.74) * mm});
            skArc(sketch, "E238.MirrorCS", {"start": v(8.59, 10.13) * mm, "mid": v(8.44, 10.3) * mm, "end": v(8.47, 10.52) * mm});
            skArc(sketch, "E239.MirrorCS", {"start": v(7.8, 11.2) * mm, "mid": v(7.89, 11.12) * mm, "end": v(7.98, 11.04) * mm});
            skLineSegment(sketch, "E240.MirrorCS", {"start": v(12.05, -0.6) * mm, "end": v(12.28, -0.45) * mm});
            skArc(sketch, "E241.MirrorCS", {"start": v(11.9, -1) * mm, "mid": v(11.92, -0.78) * mm, "end": v(12.05, -0.6) * mm});
            skLineSegment(sketch, "E242.MirrorCS", {"start": v(8.59, 10.13) * mm, "end": v(8.67, 9.86) * mm});
            skLineSegment(sketch, "E243.MirrorCS", {"start": v(12.13, 0.03) * mm, "end": v(12.28, -0.45) * mm});
            skLineSegment(sketch, "E244.MirrorCS", {"start": v(16.07, -13.2) * mm, "end": v(15.86, -13.2) * mm});
            skLineSegment(sketch, "E245.MirrorCS", {"start": v(11.37, 0.77) * mm, "end": v(11.9, -1) * mm});
            skLineSegment(sketch, "E246.MirrorCS", {"start": v(16.03, -14.91) * mm, "end": v(16.58, -14.91) * mm});
            skArc(sketch, "E247.MirrorCS", {"start": v(15.49, -15) * mm, "mid": v(15.75, -14.91) * mm, "end": v(16.03, -14.91) * mm});
            skArc(sketch, "E248.MirrorCS", {"start": v(11.72, 0.5) * mm, "mid": v(11.51, 0.6) * mm, "end": v(11.37, 0.77) * mm});
            skLineSegment(sketch, "E249.MirrorCS", {"start": v(16.53, -14.77) * mm, "end": v(16.58, -14.91) * mm});
            skLineSegment(sketch, "E250.MirrorCS", {"start": v(12, 0.5) * mm, "end": v(11.72, 0.5) * mm});
            skLineSegment(sketch, "E251.MirrorCS", {"start": v(16.03, -14.91) * mm, "end": v(16.32, -14.91) * mm});
            skArc(sketch, "E252.MirrorCS", {"start": v(9.62, 6.66) * mm, "mid": v(9.58, 7.06) * mm, "end": v(9.66, 7.45) * mm});
            skLineSegment(sketch, "E253.MirrorCS", {"start": v(12.13, 0.03) * mm, "end": v(12, 0.5) * mm});
            skArc(sketch, "E254.MirrorCS", {"start": v(15.43, -12.87) * mm, "mid": v(15.47, -12.68) * mm, "end": v(15.59, -12.52) * mm});
            skLineSegment(sketch, "E255.MirrorCS", {"start": v(16.07, -13.2) * mm, "end": v(16.53, -14.77) * mm});
            skArc(sketch, "E256.MirrorCS", {"start": v(15.86, -13.2) * mm, "mid": v(15.6, -13.1) * mm, "end": v(15.43, -12.87) * mm});
            skLineSegment(sketch, "E257.MirrorCS", {"start": v(9.03, 8.65) * mm, "end": v(9.6, 8.54) * mm});
            skArc(sketch, "E258.MirrorCS", {"start": v(15.27, -11.43) * mm, "mid": v(15.03, -11.31) * mm, "end": v(14.9, -11.09) * mm});
            skLineSegment(sketch, "E259.MirrorCS", {"start": v(15.27, -11.43) * mm, "end": v(15.54, -11.43) * mm});
            skArc(sketch, "E260.MirrorCS", {"start": v(9.03, 8.65) * mm, "mid": v(8.65, 9.2) * mm, "end": v(8.67, 9.86) * mm});
            skLineSegment(sketch, "E261.MirrorCS", {"start": v(9.1, 6.52) * mm, "end": v(8.96, 6.17) * mm});
            skLineSegment(sketch, "E262.MirrorCS", {"start": v(9.85, 7.72) * mm, "end": v(9.66, 7.45) * mm});
            skLineSegment(sketch, "E263.MirrorCS", {"start": v(15.59, -12.52) * mm, "end": v(15.86, -12.52) * mm});
            skArc(sketch, "E264.MirrorCS", {"start": v(7.8, 11.2) * mm, "mid": v(7.45, 11.29) * mm, "end": v(7.29, 11.61) * mm});
            skLineSegment(sketch, "E265.MirrorCS", {"start": v(15.32, -15.22) * mm, "end": v(15.49, -15) * mm});
            skLineSegment(sketch, "E266.MirrorCS", {"start": v(2.16, 12.96) * mm, "end": v(2.44, 12.32) * mm});
            skArc(sketch, "E267.MirrorCS", {"start": v(5.15, 13.07) * mm, "mid": v(6.25, 12.38) * mm, "end": v(7.29, 11.61) * mm});
            skFitSpline(sketch, "E268.MirrorCS", {"points": [v(3, 15.4) * mm, v(3.67, 15.4) * mm, v(4.22, 15.38) * mm, v(4.98, 15.48) * mm, v(5.98, 15.87) * mm, v(7.25, 16.46) * mm, v(8.3, 16.92) * mm, v(8.8, 17.35) * mm, v(9.17, 17.85) * mm, v(9.28, 18.38) * mm, v(9.26, 18.6) * mm, v(8.1, 18.83) * mm, v(8.18, 18.49) * mm, v(7.68, 18.6) * mm, v(7.3, 19.05) * mm, v(7.42, 19.08) * mm, v(8.36, 19.07) * mm, v(11.29, 18.68) * mm, v(13.07, 18.36) * mm, v(15.24, 17.66) * mm, v(17.6, 16.44) * mm, v(19.52, 15.06) * mm, v(20.68, 14.05) * mm, v(21.64, 12.97) * mm, v(22.19, 12.29) * mm, v(22.95, 11.24) * mm, v(23.9, 9.6) * mm, v(24.87, 7.46) * mm, v(25.3, 6.13) * mm, v(25.74, 4.27) * mm, v(25.92, 2.9) * mm, v(26.01, 1.74) * mm, v(25.98, 0.23) * mm, v(25.86, -1.54) * mm, v(25.67, -3.29) * mm, v(25.3, -4.85) * mm, v(24.7, -6.3) * mm, v(23.49, -8.96) * mm, v(22.16, -11.2) * mm, v(21.69, -11.8) * mm, v(21.8, -11.4) * mm, v(22.21, -9.27) * mm, v(22.23, -6.58) * mm, v(22.08, -5.36) * mm, v(21.33, -3.32) * mm, v(20.15, -1.95) * mm, v(18.51, -1.03) * mm, v(16.23, -0.44) * mm, v(14.42, -0.22) * mm, v(14.66, -0.16) * mm, v(15.35, 0.6) * mm, v(16.01, 1.48) * mm, v(16.8, 3.08) * mm, v(17.03, 4.61) * mm, v(16.79, 5.98) * mm, v(16.08, 7.14) * mm, v(15.46, 7.46) * mm, v(15.64, 7.56) * mm, v(15.92, 8.25) * mm, v(16.1, 9.53) * mm, v(15.66, 11.04) * mm, v(14.71, 12.08) * mm, v(12.92, 12.78) * mm, v(12.82, 12.63) * mm, v(12.8, 12.8) * mm, v(12.53, 13.26) * mm, v(11.32, 14.08) * mm, v(10.28, 14.35) * mm, v(8.88, 14.25) * mm, v(7.35, 13.47) * mm, v(6.57, 12.71) * mm, v(6.37, 12.3) * mm], "startDerivative": vector(66.18, 0.33) * mm, "endDerivative": vector(-17.3, -46.6) * mm});
            skPoint(sketch, "E269.MirrorP", {"position": v(16.02, -13.95) * mm});
            skFitSpline(sketch, "E270.MirrorCS", {"points": [v(13.15, -1.08) * mm, v(13.15, -3.4) * mm], "startDerivative": vector(0, -2.5) * mm, "endDerivative": vector(0, -2.5) * mm});
            skLineSegment(sketch, "E271.MirrorCS", {"start": v(2.16, 12.96) * mm, "end": v(0, 12.95) * mm});
            skArc(sketch, "E272.MirrorCS", {"start": v(1.94, 13.93) * mm, "mid": v(3.6, 13.71) * mm, "end": v(5.15, 13.07) * mm});
            skLineSegment(sketch, "E273.MirrorCS", {"start": v(1.94, 13.93) * mm, "end": v(0, 13.92) * mm});
            skArc(sketch, "E274.MirrorCS", {"start": v(0, 18.1) * mm, "mid": v(2.53, 16.74) * mm, "end": v(2.77, 13.88) * mm});
            skFitSpline(sketch, "E275.MirrorCS", {"points": [v(3, 15.4) * mm, v(3.67, 15.4) * mm, v(4.22, 15.38) * mm, v(4.98, 15.48) * mm, v(5.98, 15.87) * mm, v(7.25, 16.46) * mm, v(8.3, 16.92) * mm, v(8.8, 17.35) * mm, v(9.17, 17.85) * mm, v(9.28, 18.38) * mm, v(9.26, 18.6) * mm, v(8.1, 18.83) * mm, v(8.18, 18.49) * mm, v(7.68, 18.6) * mm, v(7.3, 19.05) * mm, v(7.42, 19.08) * mm, v(8.36, 19.07) * mm, v(11.29, 18.68) * mm, v(13.07, 18.36) * mm, v(15.24, 17.66) * mm, v(17.6, 16.44) * mm, v(19.52, 15.06) * mm, v(20.68, 14.05) * mm, v(21.64, 12.97) * mm, v(22.19, 12.29) * mm, v(22.95, 11.24) * mm, v(23.9, 9.6) * mm, v(24.87, 7.46) * mm, v(25.3, 6.13) * mm, v(25.74, 4.27) * mm, v(25.92, 2.9) * mm, v(26.01, 1.74) * mm, v(25.98, 0.23) * mm, v(25.86, -1.54) * mm, v(25.67, -3.29) * mm, v(25.3, -4.85) * mm, v(24.7, -6.3) * mm, v(23.49, -8.96) * mm, v(22.16, -11.2) * mm, v(21.69, -11.8) * mm, v(21.8, -11.4) * mm, v(22.21, -9.27) * mm, v(22.23, -6.58) * mm, v(22.08, -5.36) * mm, v(21.33, -3.32) * mm, v(20.15, -1.95) * mm, v(18.51, -1.03) * mm, v(16.23, -0.44) * mm, v(14.42, -0.22) * mm, v(14.66, -0.16) * mm, v(15.35, 0.6) * mm, v(16.01, 1.48) * mm, v(16.8, 3.08) * mm, v(17.03, 4.61) * mm, v(16.79, 5.98) * mm, v(16.08, 7.14) * mm, v(15.46, 7.46) * mm, v(15.64, 7.56) * mm, v(15.92, 8.25) * mm, v(16.1, 9.53) * mm, v(15.66, 11.04) * mm, v(14.71, 12.08) * mm, v(12.92, 12.78) * mm, v(12.82, 12.63) * mm, v(12.8, 12.8) * mm, v(12.53, 13.26) * mm, v(11.32, 14.08) * mm, v(10.28, 14.35) * mm, v(8.88, 14.25) * mm, v(7.35, 13.47) * mm, v(6.57, 12.71) * mm, v(6.37, 12.3) * mm], "startDerivative": vector(66.18, 0.33) * mm, "endDerivative": vector(-17.3, -46.6) * mm});
            skPoint(sketch, "E276.MirrorP", {"position": v(7.33, 10.87) * mm});
            skPoint(sketch, "E277.MirrorP", {"position": v(8.14, 9.75) * mm});
            skPoint(sketch, "E278.MirrorP", {"position": v(11.45, 0.5) * mm});
            skPoint(sketch, "E279.MirrorP", {"position": v(3.46, 12.96) * mm});
            skArc(sketch, "E280.MirrorCS", {"start": v(2.44, 12.32) * mm, "mid": v(6.53, 10.13) * mm, "end": v(8.96, 6.17) * mm});
            skLineSegment(sketch, "E281.MirrorCS", {"start": v(2.27, -8.6) * mm, "end": v(0, -8.6) * mm, "construction": true});
            skLineSegment(sketch, "E282.MirrorCS", {"start": v(0, 0.03) * mm, "end": v(16.93, 0.03) * mm, "construction": true});
            skPoint(sketch, "E283.MirrorP", {"position": v(5.02, 12.29) * mm});
            skPoint(sketch, "E284.MirrorP", {"position": v(2.27, -7.58) * mm});
            skPoint(sketch, "E285.MirrorP", {"position": v(9.47, 7.18) * mm});
            skPoint(sketch, "E286.MirrorP", {"position": v(9.06, 8.54) * mm});
            skPoint(sketch, "E287.MirrorP", {"position": v(15.75, -13.95) * mm});
            skPoint(sketch, "E288.MirrorP", {"position": v(12.05, -0.6) * mm});
            skLineSegment(sketch, "E289.MirrorCS", {"start": v(11.9, -1) * mm, "end": v(14.9, -11.09) * mm});
            skPoint(sketch, "E290.MirrorP", {"position": v(2.83, 12.93) * mm});
            skLineSegment(sketch, "E291.MirrorCS", {"start": v(9.62, 6.66) * mm, "end": v(11.37, 0.77) * mm});
            skLineSegment(sketch, "E292.MirrorCS", {"start": v(13.88, -10.4) * mm, "end": v(15.32, -15.22) * mm});
            skPoint(sketch, "E293.MirrorP", {"position": v(16.29, -13.95) * mm});
            skPoint(sketch, "E294.MirrorP", {"position": v(2.27, -9.6) * mm});
            skPoint(sketch, "E295.MirrorP", {"position": v(3.46, 13.93) * mm});
            skPoint(sketch, "E296.MirrorP", {"position": v(15, -11.43) * mm});
            skLineSegment(sketch, "E297.MirrorCS", {"start": v(8.96, 6.17) * mm, "end": v(13.88, -10.4) * mm});
            skLineSegment(sketch, "E298.MirrorCS", {"start": v(9.09, 10.28) * mm, "end": v(15.86, -12.52) * mm});
            skArc(sketch, "E299", {"start": v(-2.44, 12.32) * mm, "mid": v(0, 11.08) * mm, "end": v(2.44, 12.32) * mm});
            skSolve(sketch);
        }
        {
            var Q0;
            {var subQ0=sQuery(id+"F8.wireOp",EDGE,"E231");Q0=makeQuery(id+"F8.imprint","IMPRINT",FACE,{"disambiguationData":[TD([[makeQuery(id+"F8.imprint","IMPRINT",EDGE,{"derivedFrom":subQ0}),1.0]])]});}
            var Q1;
            Q1=makeQuery(id+"F8.imprint","IMPRINT",FACE,{"disambiguationData":[TD([[makeQuery(id+"F8.imprint","IMPRINT",EDGE,{"derivedFrom":sQuery(id+"F8.wireOp",EDGE,"E234.MirrorCS")}),-1.0]])]});
            extrude(context, id + "F9", {"entities" : qUnion([Q0, Q1]), "endBound" : BoundingType.SYMMETRIC, "depth" : 3 * mm, "offsetDistance" : 25 * mm});
        }
        {
            var Q0;
            {var subQ4=sQuery(id+"F8.wireOp",EDGE,"E181.filletArc");var subQ5=sQuery(id+"F8.wireOp",EDGE,"E178");var subQ6=makeQuery(id+"F8.imprint","INTERSECT",VERTEX,{"derivedFrom":[subQ5,subQ4]});Q0=makeQuery(id+"F8.imprint","IMPRINT",FACE,{"disambiguationData":[TD([[makeQuery(id+"F8.imprint","IMPRINT",EDGE,{"disambiguationData":[TD([[subQ6,-1.0]])],"derivedFrom":subQ5}),1.0]])]});}
            var Q1;
            {var subQ5=sQuery(id+"F8.wireOp",EDGE,"E230");var subQ6=sQuery(id+"F8.wireOp",EDGE,"E171");var subQ7=makeQuery(id+"F8.imprint","INTERSECT",VERTEX,{"derivedFrom":[subQ6,subQ5]});Q1=makeQuery(id+"F8.imprint","IMPRINT",FACE,{"disambiguationData":[TD([[makeQuery(id+"F8.imprint","IMPRINT",EDGE,{"disambiguationData":[TD([[subQ7,-1.0]])],"derivedFrom":subQ6}),1.0]])]});}
            extrude(context, id + "F10", {"entities" : qUnion([Q0, Q1]), "endBound" : BoundingType.SYMMETRIC, "depth" : 5 * mm, "offsetDistance" : 25 * mm});
        }
        {
            var Q0;
            {var subQ2=sQuery(id+"F8.wireOp",EDGE,"E222");Q0=makeQuery(id+"F8.imprint","IMPRINT",FACE,{"disambiguationData":[TD([[makeQuery(id+"F8.imprint","IMPRINT",EDGE,{"derivedFrom":subQ2}),1.0]])]});}
            extrude(context, id + "F11", {"entities" : qUnion([Q0]), "operationType" : NewBodyOperationType.ADD, "endBound" : BoundingType.SYMMETRIC, "depth" : 3 * mm, "offsetDistance" : 25 * mm});
        }
        {
            var Q0;
            Q0=sQuery(id+"F0.wireOp",EDGE,"E145.MirrorCS");
            cPlane(context, id + "F12", {"entities" : qUnion([Q0]), "cplaneType" : CPlaneType.LINE_ANGLE, "offset" : 25 * mm, "angle" : 0 * degree, "width" : 150 * mm, "height" : 150 * mm});
        }
        {
            var Q0;
            Q0=qCreatedBy(id+"F12.planeOp",FACE);
            var sketch = newSketch(context, id + "F13", { "sketchPlane" : qUnion([Q0])});
            skCircle(sketch, "E300", {"center": v(0, -4.22) * mm, "radius": 5.98 * mm});
            skCircle(sketch, "E301", {"center": v(0, -4.22) * mm, "radius": 1.4 * mm});
            skSolve(sketch);
        }
        {
            var Q0;
            Q0=makeQuery(id+"F13.imprint","IMPRINT",FACE,{"disambiguationData":[TD([[makeQuery(id+"F13.imprint","IMPRINT",EDGE,{"derivedFrom":sQuery(id+"F13.wireOp",EDGE,"E301")}),1.0]])]});
            extrude(context, id + "F14", {"entities" : qUnion([Q0]), "oppositeDirection" : true, "depth" : 1 * mm, "offsetDistance" : 25 * mm});
        }
        {
            var Q0;
            Q0=makeQuery(id+"F13.imprint","IMPRINT",FACE,{"disambiguationData":[TD([[makeQuery(id+"F13.imprint","IMPRINT",EDGE,{"derivedFrom":sQuery(id+"F13.wireOp",EDGE,"E300")}),1.0]])]});
            extrude(context, id + "F15", {"entities" : qUnion([Q0]), "operationType" : NewBodyOperationType.ADD, "endBound" : BoundingType.UP_TO_NEXT, "depth" : 25 * mm, "offsetDistance" : 25 * mm});
        }
    });
